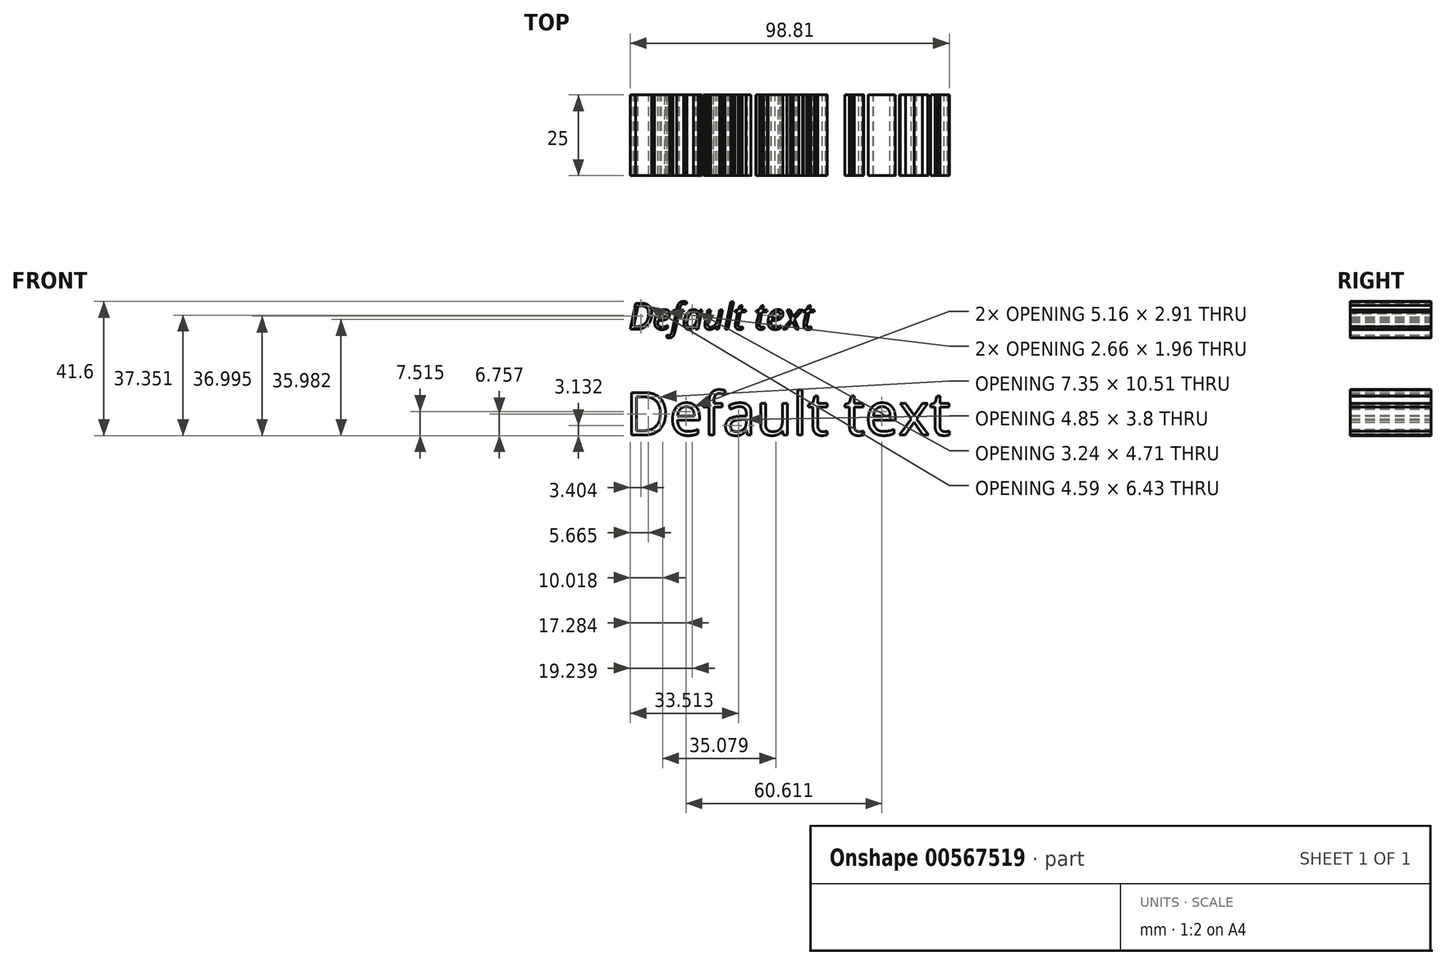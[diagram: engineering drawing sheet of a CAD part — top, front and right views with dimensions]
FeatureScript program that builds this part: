
annotation { "Feature Type Name" : "Feature", "Feature Type Description" : "" }
export const myFeature = defineFeature(function(context is Context, id is Id, definition is map)
    precondition{}
    {
        {
            var Q0;
            Q0=qCreatedBy(makeId("Front.planeOp"),FACE);
            var sketch = newSketch(context, id + "F0", { "sketchPlane" : qUnion([Q0])});
            skPoint(sketch, "E0", {"position": v(-23.14, 0) * mm});
            skPoint(sketch, "E1", {"position": v(10.2, 42.83) * mm});
            skPoint(sketch, "E2", {"position": v(13.85, -24.95) * mm});
            skPoint(sketch, "E3", {"position": v(-15.97, 13.27) * mm});
            skPoint(sketch, "E4", {"position": v(-34.8, -21.48) * mm});
            skText(sketch, "E5", { "text": "Default text", "fontName": "OpenSans-Regular.ttf"});
            skText(sketch, "E6", { "text": "Default text", "fontName": "OpenSans-Italic.ttf"});
            const initialGuessF0  = {"E5": [-0.05408, 0, 1, 0, 0.01327], "E6": [-0.0532, 0.03279, 1, 0, 0.00812]};
            skSetInitialGuess(sketch, initialGuessF0);
            skSolve(sketch);
        }
        {
            var Q0;
            Q0 = qSketchRegion(id + "F0", true);
            extrude(context, id + "F1", {"entities" : qUnion([Q0]), "endBound" : BoundingType.SYMMETRIC, "depth" : 25 * mm, "offsetDistance" : 25 * mm});
        }
    });
